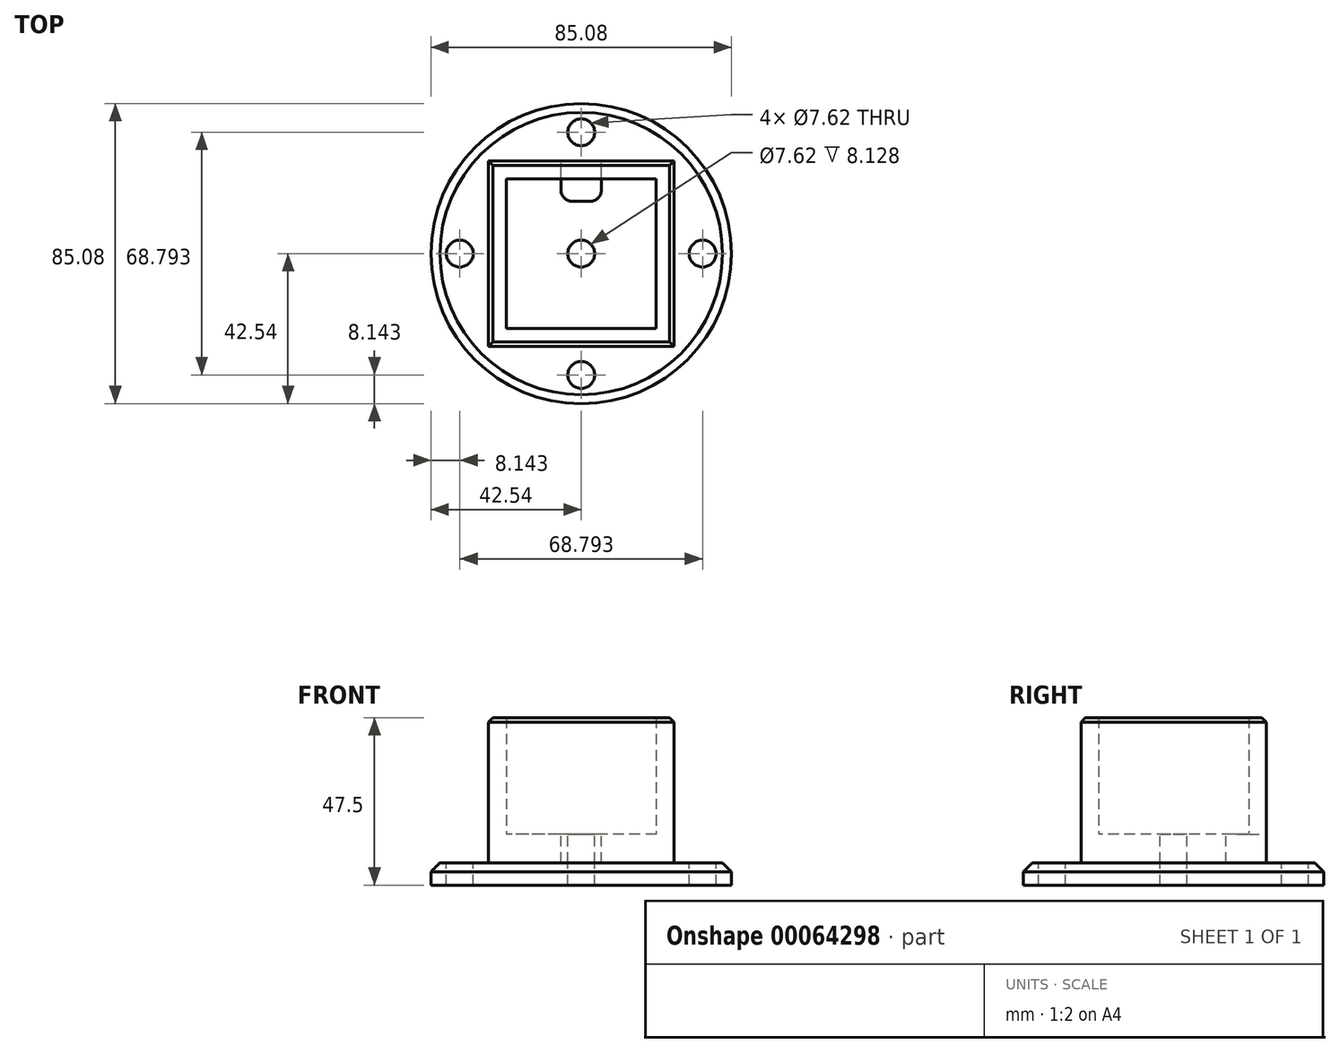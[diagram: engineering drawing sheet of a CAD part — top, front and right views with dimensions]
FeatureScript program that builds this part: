
annotation { "Feature Type Name" : "Feature", "Feature Type Description" : "" }
export const myFeature = defineFeature(function(context is Context, id is Id, definition is map)
    precondition{}
    {
        {
            var Q0;
            Q0=qCreatedBy(makeId("Top.planeOp"),FACE);
            var sketch = newSketch(context, id + "F0", { "sketchPlane" : qUnion([Q0])});
            skLineSegment(sketch, "E0.rect.bottom", {"start": v(21.25, 21.25) * mm, "end": v(-21.25, 21.25) * mm});
            skLineSegment(sketch, "E0.rect.top", {"start": v(21.25, -21.25) * mm, "end": v(-21.25, -21.25) * mm});
            skLineSegment(sketch, "E0.rect.left", {"start": v(21.25, 21.25) * mm, "end": v(21.25, -21.25) * mm});
            skLineSegment(sketch, "E0.rect.right", {"start": v(-21.25, 21.25) * mm, "end": v(-21.25, -21.25) * mm});
            skPoint(sketch, "E0.rect.middle", {"position": v(0, 0) * mm});
            skLineSegment(sketch, "E1.rect.bottom", {"start": v(26.25, 26.25) * mm, "end": v(-26.25, 26.25) * mm});
            skLineSegment(sketch, "E1.rect.top", {"start": v(26.25, -26.25) * mm, "end": v(-26.25, -26.25) * mm});
            skLineSegment(sketch, "E1.rect.left", {"start": v(26.25, 26.25) * mm, "end": v(26.25, -26.25) * mm});
            skLineSegment(sketch, "E1.rect.right", {"start": v(-26.25, 26.25) * mm, "end": v(-26.25, -26.25) * mm});
            skLineSegment(sketch, "E2", {"start": v(21.25, 0) * mm, "end": v(26.25, 0) * mm, "construction": true});
            skSolve(sketch);
        }
        {
            var Q0;
            Q0=makeQuery(id+"F0.imprint","IMPRINT",FACE,{"disambiguationData":[TD([[makeQuery(id+"F0.imprint","IMPRINT",EDGE,{"derivedFrom":sQuery(id+"F0.wireOp",EDGE,"E0.rect.bottom")}),-1.0]])]});
            extrude(context, id + "F1", {"entities" : qUnion([Q0]), "depth" : 33.02 * mm});
        }
        {
            var Q0;
            Q0=makeQuery(id+"F1.opExtrude","CAP_FACE",FACE,{"disambiguationData":[OSD([sQuery(id+"F0.wireOp",EDGE,"E0.rect.bottom"),sQuery(id+"F0.wireOp",EDGE,"E0.rect.top"),sQuery(id+"F0.wireOp",EDGE,"E0.rect.left"),sQuery(id+"F0.wireOp",EDGE,"E0.rect.right"),sQuery(id+"F0.wireOp",EDGE,"E1.rect.bottom"),sQuery(id+"F0.wireOp",EDGE,"E1.rect.top"),sQuery(id+"F0.wireOp",EDGE,"E1.rect.left"),sQuery(id+"F0.wireOp",EDGE,"E1.rect.right")])],"isStart":true});
            var sketch = newSketch(context, id + "F2", { "sketchPlane" : qUnion([Q0])});
            skLineSegment(sketch, "E3.bottom", {"start": v(-26.25, 26.25) * mm, "end": v(26.25, 26.25) * mm});
            skLineSegment(sketch, "E3.top", {"start": v(-26.25, -26.25) * mm, "end": v(26.25, -26.25) * mm});
            skLineSegment(sketch, "E3.left", {"start": v(-26.25, 26.25) * mm, "end": v(-26.25, -26.25) * mm});
            skLineSegment(sketch, "E3.right", {"start": v(26.25, 26.25) * mm, "end": v(26.25, -26.25) * mm});
            skCircle(sketch, "E4", {"center": v(0, 0) * mm, "radius": 3.81 * mm});
            skLineSegment(sketch, "E5.bottom", {"start": v(-2.54, -14.82) * mm, "end": v(2.54, -14.82) * mm});
            skLineSegment(sketch, "E5.top", {"start": v(-5.72, -26.25) * mm, "end": v(5.71, -26.25) * mm});
            skLineSegment(sketch, "E5.left", {"start": v(-5.72, -18) * mm, "end": v(-5.72, -26.25) * mm});
            skLineSegment(sketch, "E5.right", {"start": v(5.71, -18) * mm, "end": v(5.71, -26.25) * mm});
            skPoint(sketch, "E6", {"position": v(0, -26.25) * mm});
            skPoint(sketch, "E7.visualSharp", {"position": v(-5.72, -14.82) * mm});
            skArc(sketch, "E7.filletArc", {"start": v(-2.54, -14.82) * mm, "mid": v(-4.79, -15.75) * mm, "end": v(-5.72, -18) * mm});
            skPoint(sketch, "E8.visualSharp", {"position": v(5.71, -14.82) * mm});
            skArc(sketch, "E8.filletArc", {"start": v(5.71, -18) * mm, "mid": v(4.79, -15.75) * mm, "end": v(2.54, -14.82) * mm});
            skSolve(sketch);
        }
        {
            var Q0;
            Q0=makeQuery(id+"F2.imprint","IMPRINT",FACE,{"disambiguationData":[TD([[makeQuery(id+"F2.imprint","IMPRINT",EDGE,{"derivedFrom":sQuery(id+"F2.wireOp",EDGE,"E3.bottom")}),1.0]])]});
            var Q1;
            Q1=makeQuery(id+"F2.imprint","IMPRINT",FACE,{"disambiguationData":[TD([[makeQuery(id+"F2.imprint","IMPRINT",EDGE,{"derivedFrom":sQuery(id+"F2.wireOp",EDGE,"E4")}),-1.0]])]});
            var Q2;
            Q2=makeQuery(id+"F1.opExtrude","CAP_FACE",FACE,{"disambiguationData":[OSD([sQuery(id+"F0.wireOp",EDGE,"E0.rect.bottom"),sQuery(id+"F0.wireOp",EDGE,"E0.rect.top"),sQuery(id+"F0.wireOp",EDGE,"E0.rect.left"),sQuery(id+"F0.wireOp",EDGE,"E0.rect.right"),sQuery(id+"F0.wireOp",EDGE,"E1.rect.bottom"),sQuery(id+"F0.wireOp",EDGE,"E1.rect.top"),sQuery(id+"F0.wireOp",EDGE,"E1.rect.left"),sQuery(id+"F0.wireOp",EDGE,"E1.rect.right")])],"isStart":false});
            extrude(context, id + "F3", {"entities" : qUnion([Q0, Q1, Q2]), "operationType" : NewBodyOperationType.ADD, "depth" : 8.13 * mm});
        }
        {
            var Q0;
            Q0=makeQuery(id+"F3.opExtrude","CAP_FACE",FACE,{"disambiguationData":[OSD([sQuery(id+"F2.wireOp",EDGE,"E3.bottom"),sQuery(id+"F2.wireOp",EDGE,"E3.top"),sQuery(id+"F2.wireOp",EDGE,"E3.left"),sQuery(id+"F2.wireOp",EDGE,"E3.right"),sQuery(id+"F2.wireOp",EDGE,"E4"),sQuery(id+"F2.wireOp",EDGE,"E5.bottom"),sQuery(id+"F2.wireOp",EDGE,"E5.left"),sQuery(id+"F2.wireOp",EDGE,"E5.right"),sQuery(id+"F2.wireOp",EDGE,"E7.filletArc"),sQuery(id+"F2.wireOp",EDGE,"E8.filletArc")])],"isStart":false});
            var sketch = newSketch(context, id + "F4", { "sketchPlane" : qUnion([Q0])});
            skCircle(sketch, "E9", {"center": v(0, 0) * mm, "radius": 42.54 * mm});
            skSolve(sketch);
        }
        {
            var Q0;
            Q0 = qSketchRegion(id + "F4", true);
            extrude(context, id + "F5", {"entities" : qUnion([Q0]), "operationType" : NewBodyOperationType.ADD, "depth" : 6.35 * mm});
        }
        {
            var Q0;
            Q0=makeQuery(id+"F1.opExtrude","CAP_EDGE",EDGE,{"disambiguationData":[OSD([sQuery(id+"F0.wireOp",EDGE,"E1.rect.left")])],"isStart":false});
            var Q1;
            Q1=makeQuery(id+"F1.opExtrude","CAP_EDGE",EDGE,{"disambiguationData":[OSD([sQuery(id+"F0.wireOp",EDGE,"E1.rect.bottom")])],"isStart":false});
            var Q2;
            Q2=makeQuery(id+"F1.opExtrude","CAP_EDGE",EDGE,{"disambiguationData":[OSD([sQuery(id+"F0.wireOp",EDGE,"E1.rect.right")])],"isStart":false});
            var Q3;
            Q3=makeQuery(id+"F1.opExtrude","CAP_EDGE",EDGE,{"disambiguationData":[OSD([sQuery(id+"F0.wireOp",EDGE,"E1.rect.top")])],"isStart":false});
            chamfer(context, id + "F6", {"entities" : qUnion([Q0, Q1, Q2, Q3]), "width" : 1.27 * mm, "tangentPropagation" : true});
        }
        {
            var Q0;
            Q0=makeQuery(id+"F4.imprint","IMPRINT",FACE,{"disambiguationData":[TD([[makeQuery(id+"F4.imprint","IMPRINT",EDGE,{"derivedFrom":sQuery(id+"F4.wireOp",EDGE,"E9")}),1.0]])]});
            var sketch = newSketch(context, id + "F7", { "sketchPlane" : qUnion([Q0])});
            skLineSegment(sketch, "E10.0", {"start": v(26.25, -26.25) * mm, "end": v(26.25, 26.25) * mm});
            skLineSegment(sketch, "E10.1", {"start": v(26.25, 26.25) * mm, "end": v(-26.25, 26.25) * mm});
            skCircle(sketch, "E11.0", {"center": v(0, 0) * mm, "radius": 42.54 * mm});
            skLineSegment(sketch, "E12", {"start": v(26.25, 0) * mm, "end": v(42.54, 0) * mm, "construction": true});
            skCircle(sketch, "E13", {"center": v(34.4, 0) * mm, "radius": 3.81 * mm});
            skCircle(sketch, "E14.1.0", {"center": v(0, 34.4) * mm, "radius": 3.81 * mm});
            skCircle(sketch, "E14.2.0", {"center": v(-34.4, 0) * mm, "radius": 3.81 * mm});
            skCircle(sketch, "E14.3.0", {"center": v(0, -34.4) * mm, "radius": 3.81 * mm});
            skSolve(sketch);
        }
        {
            var Q0;
            Q0=makeQuery(id+"F7.imprint","IMPRINT",FACE,{"disambiguationData":[TD([[makeQuery(id+"F7.imprint","IMPRINT",EDGE,{"derivedFrom":sQuery(id+"F7.wireOp",EDGE,"E14.1.0")}),1.0]])]});
            var Q1;
            Q1=makeQuery(id+"F7.imprint","IMPRINT",FACE,{"disambiguationData":[TD([[makeQuery(id+"F7.imprint","IMPRINT",EDGE,{"derivedFrom":sQuery(id+"F7.wireOp",EDGE,"E13")}),1.0]])]});
            var Q2;
            Q2=makeQuery(id+"F7.imprint","IMPRINT",FACE,{"disambiguationData":[TD([[makeQuery(id+"F7.imprint","IMPRINT",EDGE,{"derivedFrom":sQuery(id+"F7.wireOp",EDGE,"E14.3.0")}),1.0]])]});
            var Q3;
            Q3=makeQuery(id+"F7.imprint","IMPRINT",FACE,{"disambiguationData":[TD([[makeQuery(id+"F7.imprint","IMPRINT",EDGE,{"derivedFrom":sQuery(id+"F7.wireOp",EDGE,"E14.2.0")}),1.0]])]});
            extrude(context, id + "F8", {"entities" : qUnion([Q0, Q1, Q2, Q3]), "operationType" : NewBodyOperationType.REMOVE, "endBound" : BoundingType.UP_TO_NEXT, "depth" : 25.4 * mm});
        }
        {
            var Q0;
            Q0=makeQuery(id+"F5.opExtrude","CAP_EDGE",EDGE,{"disambiguationData":[OSD([sQuery(id+"F4.wireOp",EDGE,"E9")])],"isStart":true});
            chamfer(context, id + "F9", {"entities" : qUnion([Q0]), "width" : 2.54 * mm, "tangentPropagation" : true});
        }
    });
